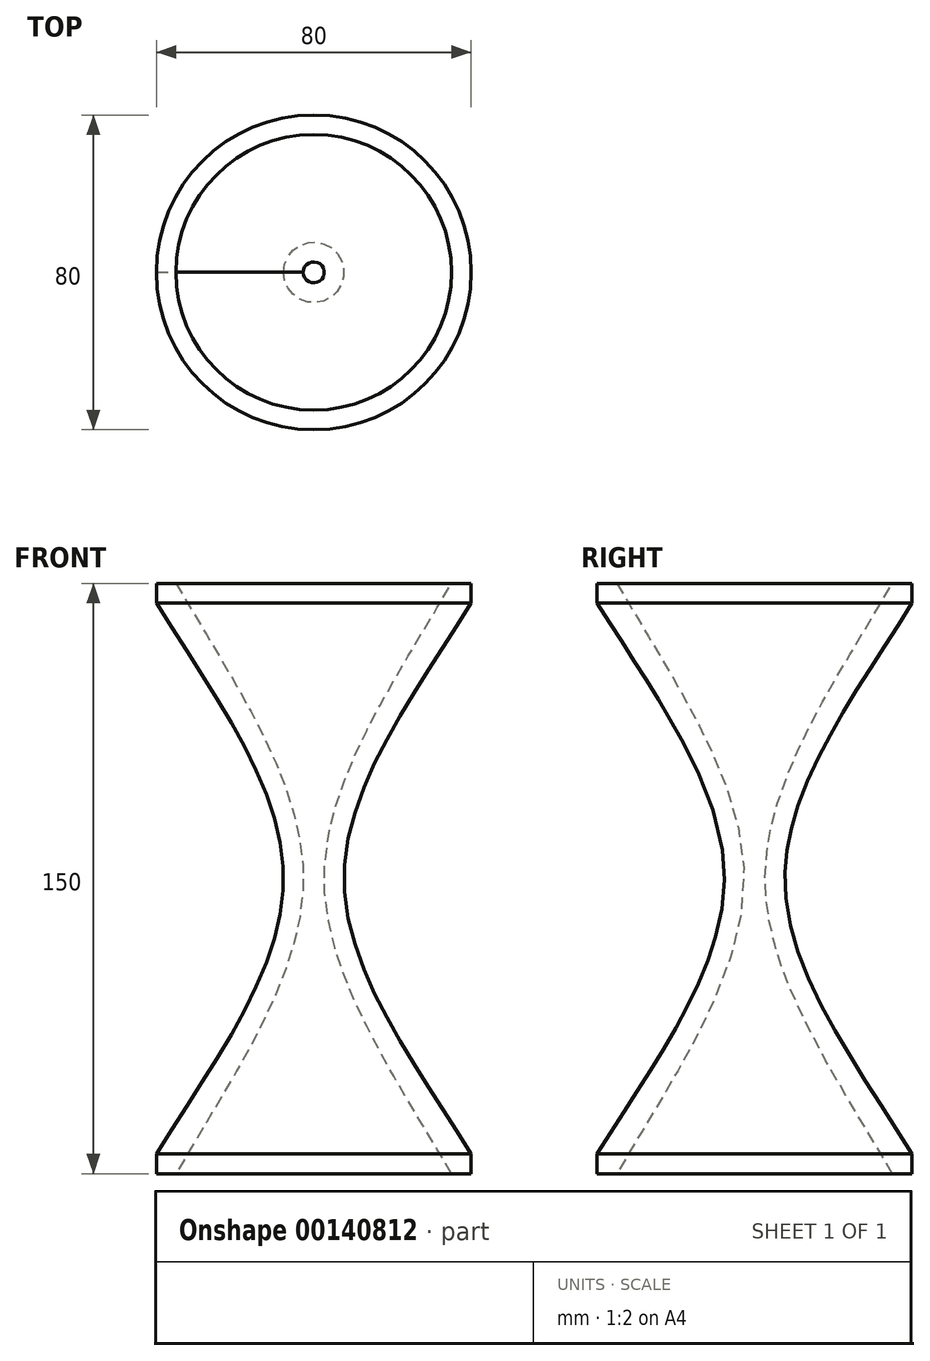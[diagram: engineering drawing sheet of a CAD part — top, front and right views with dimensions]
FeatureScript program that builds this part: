
annotation { "Feature Type Name" : "Feature", "Feature Type Description" : "" }
export const myFeature = defineFeature(function(context is Context, id is Id, definition is map)
    precondition{}
    {
        {
            var Q0;
            Q0=qCreatedBy(makeId("Front.planeOp"),FACE);
            var sketch = newSketch(context, id + "F0", { "sketchPlane" : qUnion([Q0])});
            skLineSegment(sketch, "E0", {"start": v(0, 0) * mm, "end": v(0, 70) * mm, "construction": true});
            skLineSegment(sketch, "E1", {"start": v(0, 70) * mm, "end": v(-40, 70) * mm, "construction": true});
            skLineSegment(sketch, "E2", {"start": v(-40, 70) * mm, "end": v(-40, 75) * mm});
            skLineSegment(sketch, "E3.MirrorCS", {"start": v(-40, -70) * mm, "end": v(-40, -75) * mm});
            skLineSegment(sketch, "E4", {"start": v(-40, -75) * mm, "end": v(-35, -75) * mm});
            skLineSegment(sketch, "E5.MirrorCS", {"start": v(-40, 75) * mm, "end": v(-35, 75) * mm});
            skFitSpline(sketch, "E6", {"points": [v(-35, 75) * mm, v(-2.67, 0) * mm, v(-35, -75) * mm], "startDerivative": vector(86.84, -150) * mm, "endDerivative": vector(-86.84, -150) * mm});
            skFitSpline(sketch, "E7", {"points": [v(-40, 70) * mm, v(-7.67, 0) * mm, v(-40, -70) * mm], "startDerivative": vector(86.89, -140) * mm, "endDerivative": vector(-86.89, -140) * mm});
            skSolve(sketch);
        }
        {
            var Q0;
            Q0=makeQuery(id+"F0.imprint","IMPRINT",FACE,{"disambiguationData":[TD([[makeQuery(id+"F0.imprint","IMPRINT",EDGE,{"derivedFrom":sQuery(id+"F0.wireOp",EDGE,"E2")}),-1.0]])]});
            var Q1;
            Q1=sQuery(id+"F0.wireOp",EDGE,"E0");
            revolve(context, id + "F1", {"entities" : qUnion([Q0]), "axis" : qUnion([Q1]), "revolveType" : RevolveType.FULL});
        }
    });
